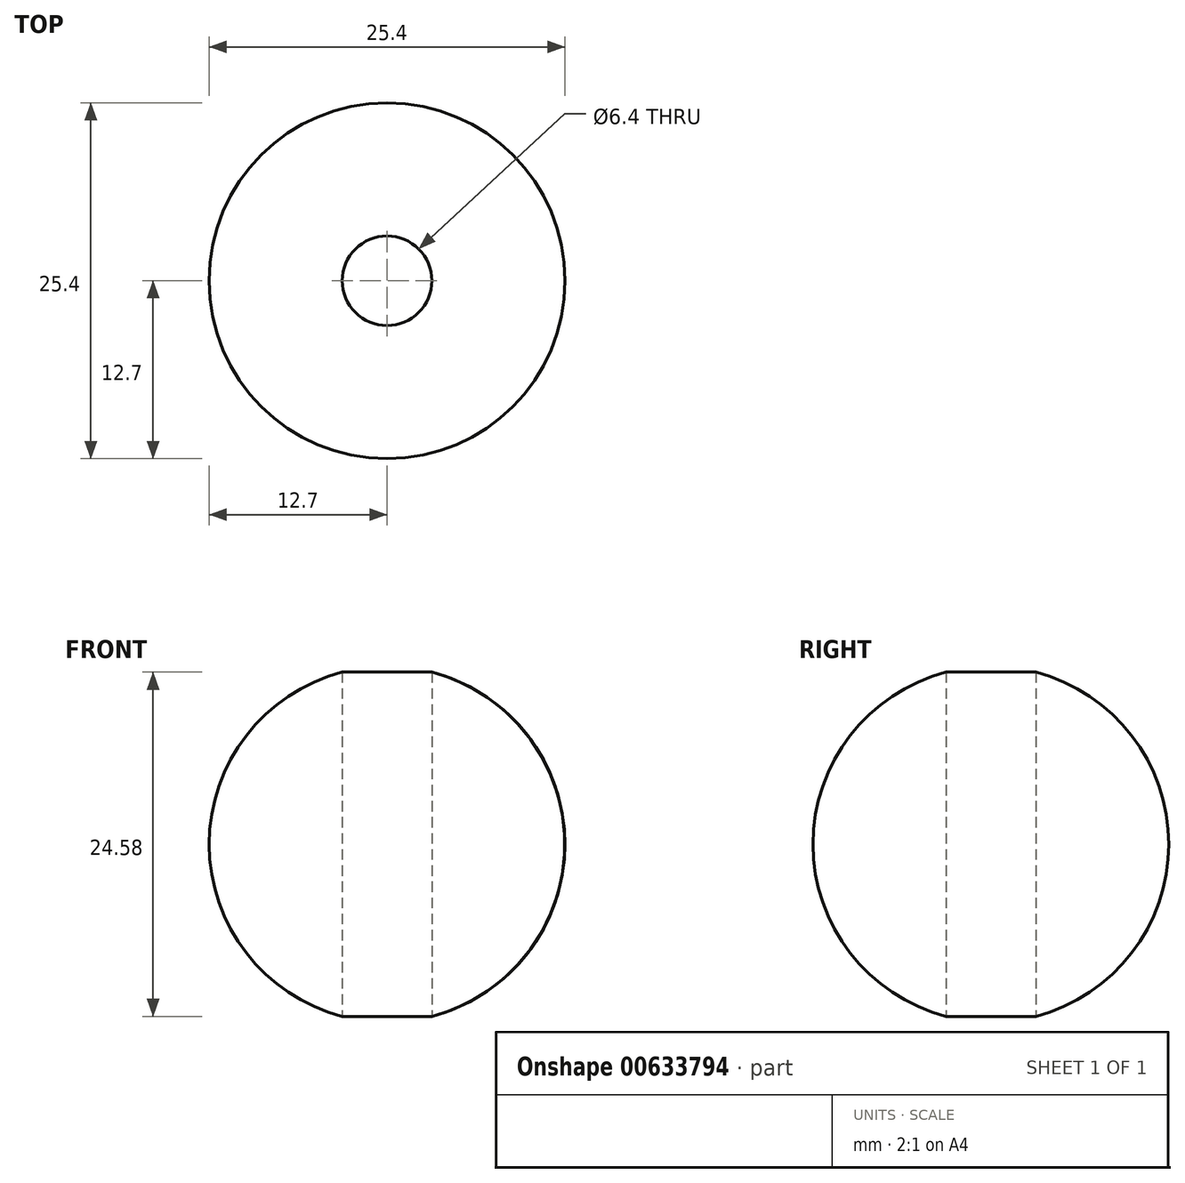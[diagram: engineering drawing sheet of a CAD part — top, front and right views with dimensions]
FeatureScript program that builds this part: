
annotation { "Feature Type Name" : "Feature", "Feature Type Description" : "" }
export const myFeature = defineFeature(function(context is Context, id is Id, definition is map)
    precondition{}
    {
        {
            var Q0;
            Q0=qCreatedBy(makeId("Top.planeOp"),FACE);
            var sketch = newSketch(context, id + "F0", { "sketchPlane" : qUnion([Q0])});
            skCircle(sketch, "E0", {"center": v(0, 0) * mm, "radius": 12.7 * mm});
            skSolve(sketch);
        }
        {
            var Q0;
            Q0 = qSketchRegion(id + "F0", true);
            var Q1;
            Q1=makeQuery(id+"F0.imprint","IMPRINT",FACE,{"disambiguationData":[TD([[makeQuery(id+"F0.imprint","IMPRINT",EDGE,{"derivedFrom":sQuery(id+"F0.wireOp",EDGE,"E0")}),1.0]])]});
            extrude(context, id + "F1", {"entities" : qUnion([Q0, Q1]), "depth" : 25.4 * mm, "offsetDistance" : 25.4 * mm});
        }
        {
            var Q0;
            Q0=makeQuery(id+"F1.opExtrude","CAP_EDGE",EDGE,{"disambiguationData":[OSD([sQuery(id+"F0.wireOp",EDGE,"E0")])],"isStart":false});
            var Q1;
            Q1=makeQuery(id+"F1.opExtrude","CAP_EDGE",EDGE,{"disambiguationData":[OSD([sQuery(id+"F0.wireOp",EDGE,"E0")])],"isStart":true});
            fillet(context, id + "F2", {"entities" : qUnion([Q0, Q1]), "radius" : 12.7 * mm, "tangentPropagation" : true, "allowEdgeOverflow" : false});
        }
        {
            var Q0;
            Q0=qCreatedBy(makeId("Top.planeOp"),FACE);
            var sketch = newSketch(context, id + "F3", { "sketchPlane" : qUnion([Q0])});
            skCircle(sketch, "E1", {"center": v(0, 0) * mm, "radius": 3.2 * mm});
            skSolve(sketch);
        }
        {
            var Q0;
            Q0=makeQuery(id+"F3.imprint","IMPRINT",FACE,{"disambiguationData":[TD([[makeQuery(id+"F3.imprint","IMPRINT",EDGE,{"derivedFrom":sQuery(id+"F3.wireOp",EDGE,"E1")}),1.0]])]});
            extrude(context, id + "F4", {"entities" : qUnion([Q0]), "operationType" : NewBodyOperationType.REMOVE, "endBound" : BoundingType.THROUGH_ALL, "depth" : 25.4 * mm, "offsetDistance" : 25.4 * mm});
        }
    });
